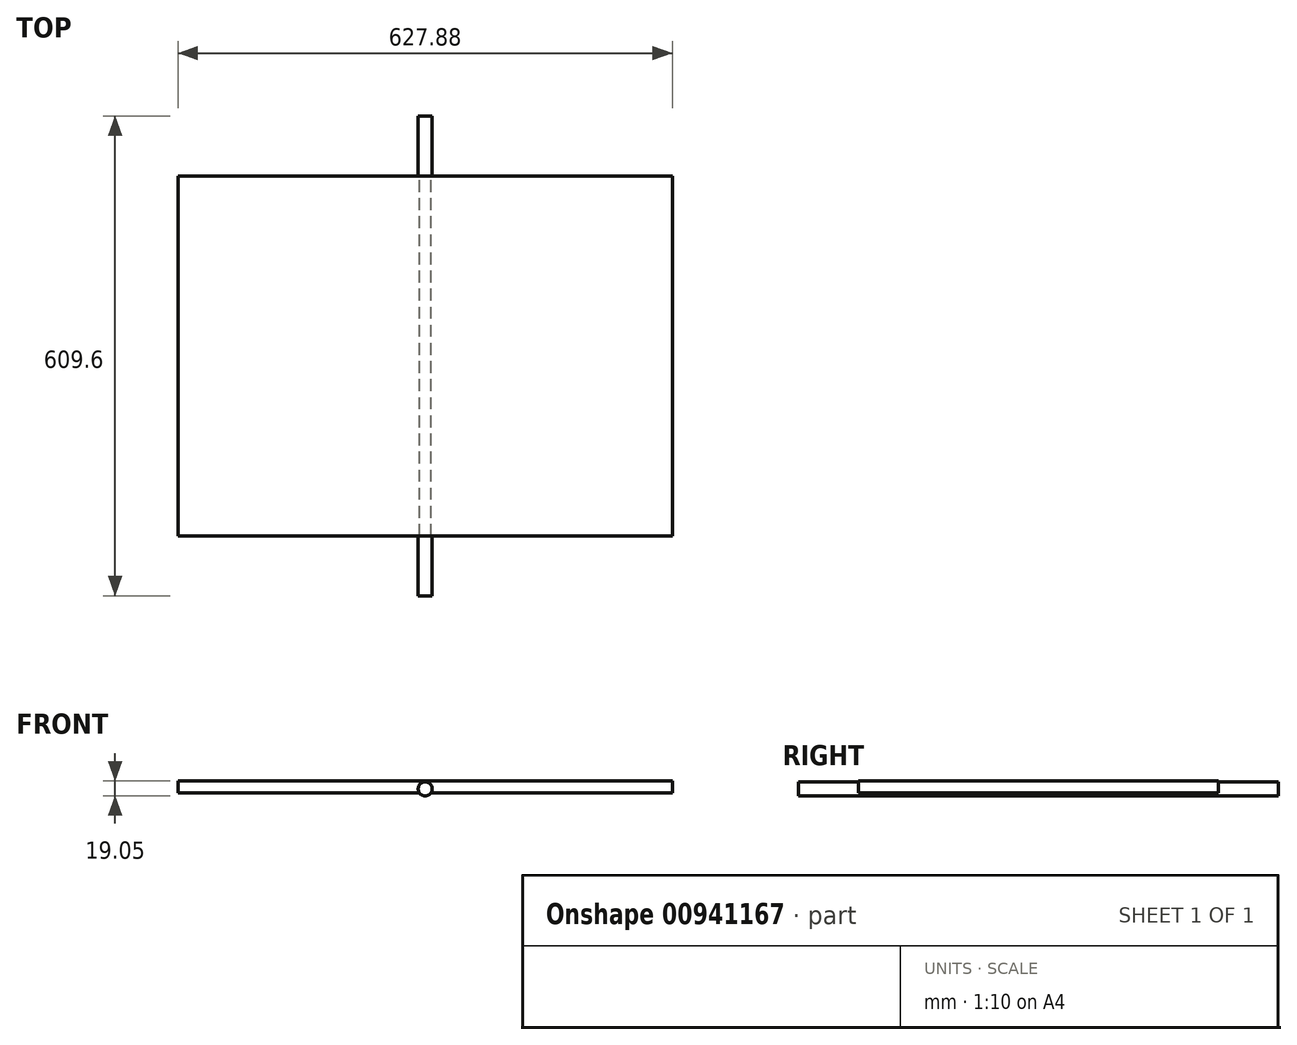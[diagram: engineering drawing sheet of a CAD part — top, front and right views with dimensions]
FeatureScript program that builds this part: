
annotation { "Feature Type Name" : "Feature", "Feature Type Description" : "" }
export const myFeature = defineFeature(function(context is Context, id is Id, definition is map)
    precondition{}
    {
        {
            var Q0;
            Q0=qCreatedBy(makeId("Front.planeOp"),FACE);
            var sketch = newSketch(context, id + "F0", { "sketchPlane" : qUnion([Q0])});
            skCircle(sketch, "E0", {"center": v(0, 0) * mm, "radius": 8.9 * mm});
            skSolve(sketch);
        }
        {
            var Q0;
            Q0 = qSketchRegion(id + "F0", true);
            extrude(context, id + "F1", {"entities" : qUnion([Q0]), "depth" : 304.8 * mm, "offsetDistance" : 25.4 * mm, "hasSecondDirection" : true, "secondDirectionOppositeDirection" : true, "secondDirectionDepth" : 304.8 * mm});
        }
        {
            var Q0;
            Q0=qCreatedBy(makeId("Top.planeOp"),FACE);
            var sketch = newSketch(context, id + "F2", { "sketchPlane" : qUnion([Q0])});
            skLineSegment(sketch, "E1.bottom", {"start": v(313.94, 228.6) * mm, "end": v(-313.94, 228.6) * mm});
            skLineSegment(sketch, "E1.top", {"start": v(313.94, -228.6) * mm, "end": v(-313.94, -228.6) * mm});
            skLineSegment(sketch, "E1.left", {"start": v(313.94, 228.6) * mm, "end": v(313.94, -228.6) * mm});
            skLineSegment(sketch, "E1.right", {"start": v(-313.94, 228.6) * mm, "end": v(-313.94, -228.6) * mm});
            skPoint(sketch, "E1.middle", {"position": v(0, 0) * mm});
            skSolve(sketch);
        }
        {
            var Q0;
            Q0 = qSketchRegion(id + "F2", true);
            extrude(context, id + "F3", {"entities" : qUnion([Q0]), "operationType" : NewBodyOperationType.ADD, "depth" : 10.16 * mm, "offsetDistance" : 25.4 * mm, "hasSecondDirection" : true, "secondDirectionOppositeDirection" : true, "secondDirectionDepth" : 5.08 * mm});
        }
    });
